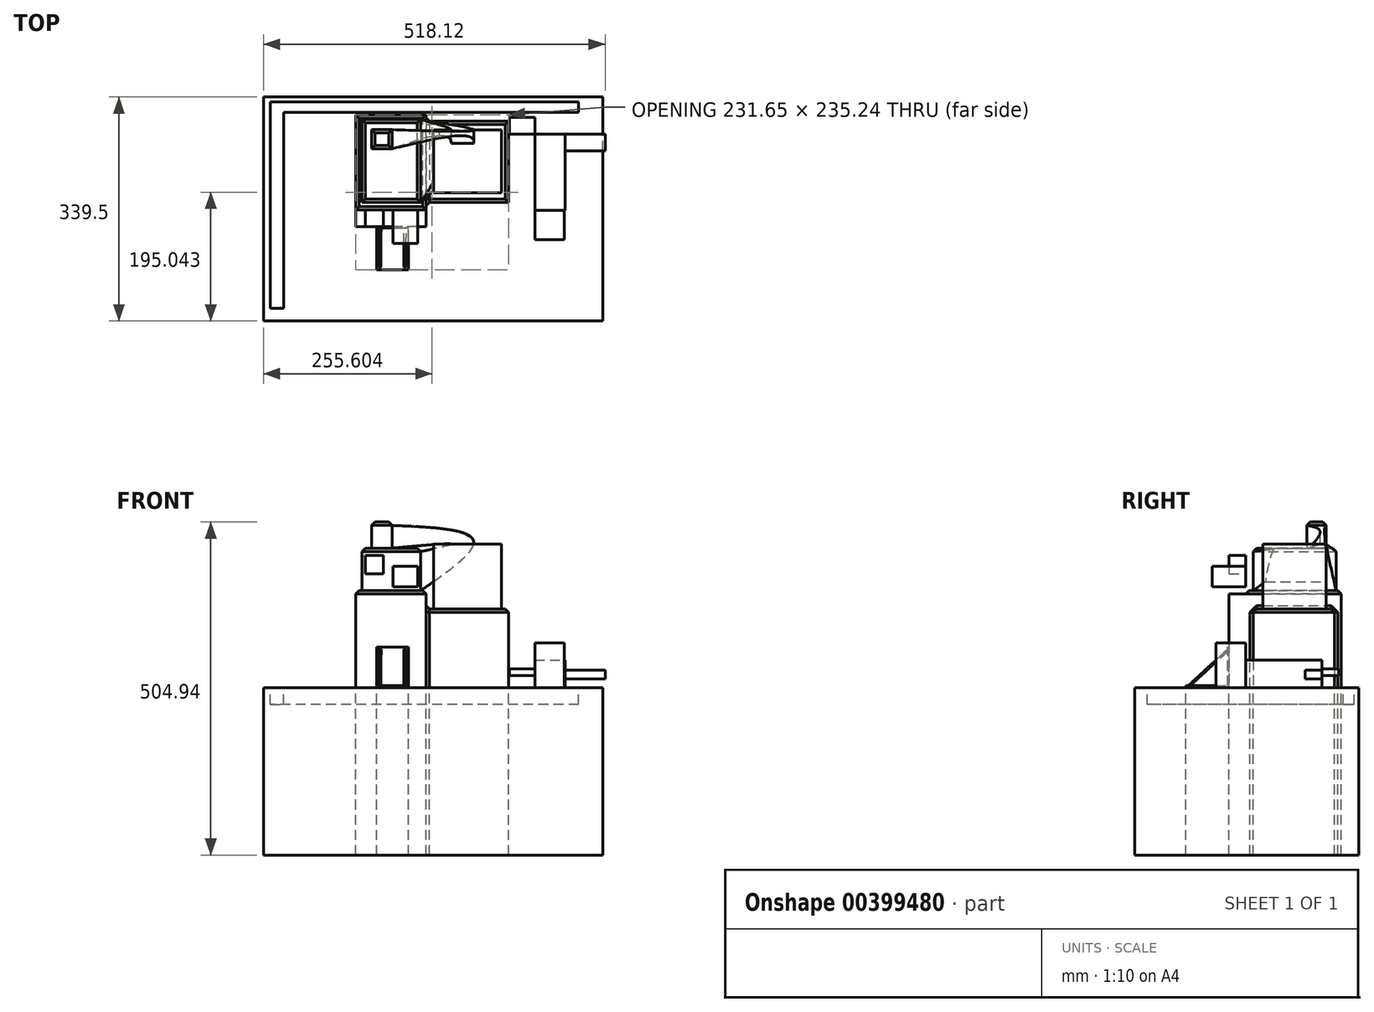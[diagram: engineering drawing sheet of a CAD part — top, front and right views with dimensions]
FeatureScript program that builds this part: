
annotation { "Feature Type Name" : "Feature", "Feature Type Description" : "" }
export const myFeature = defineFeature(function(context is Context, id is Id, definition is map)
    precondition{}
    {
        {
            var Q0;
            Q0=qCreatedBy(makeId("Right.planeOp"),FACE);
            var sketch = newSketch(context, id + "F0", { "sketchPlane" : qUnion([Q0])});
            skLineSegment(sketch, "E0.bottom", {"start": v(-92.5, 57.27) * mm, "end": v(51.8, 57.27) * mm});
            skLineSegment(sketch, "E0.top", {"start": v(-92.5, -89.79) * mm, "end": v(51.8, -89.79) * mm});
            skLineSegment(sketch, "E0.left", {"start": v(-92.5, 57.27) * mm, "end": v(-92.5, -89.79) * mm});
            skLineSegment(sketch, "E0.right", {"start": v(51.8, 57.27) * mm, "end": v(51.8, -89.79) * mm});
            skSolve(sketch);
        }
        {
            var Q0;
            Q0=makeQuery(id+"F0.imprint","IMPRINT",FACE,{"disambiguationData":[TD([[makeQuery(id+"F0.imprint","IMPRINT",EDGE,{"derivedFrom":sQuery(id+"F0.wireOp",EDGE,"E0.bottom")}),-1.0]])]});
            extrude(context, id + "F1", {"entities" : qUnion([Q0]), "depth" : 106.93 * mm});
        }
        {
            var Q0;
            Q0=makeQuery(id+"F1.opExtrude","CAP_EDGE",EDGE,{"disambiguationData":[OSD([sQuery(id+"F0.wireOp",EDGE,"E0.bottom")])],"isStart":true});
            var Q1;
            Q1=makeQuery(id+"F1.opExtrude","CAP_EDGE",EDGE,{"disambiguationData":[OSD([sQuery(id+"F0.wireOp",EDGE,"E0.bottom")])],"isStart":false});
            var Q2;
            Q2=makeQuery(id+"F1.opExtrude","SWEPT_EDGE",EDGE,{"disambiguationData":[OSD([sQuery(id+"F0.wireOp",EDGE,"E0.bottom"),sQuery(id+"F0.wireOp",EDGE,"E0.left")])]});
            var Q3;
            Q3=makeQuery(id+"F1.opExtrude","SWEPT_EDGE",EDGE,{"disambiguationData":[OSD([sQuery(id+"F0.wireOp",EDGE,"E0.bottom"),sQuery(id+"F0.wireOp",EDGE,"E0.right")])]});
            chamfer(context, id + "F2", {"entities" : qUnion([Q0, Q1, Q2, Q3]), "width" : 5.08 * mm, "tangentPropagation" : true});
        }
        {
            var Q0;
            Q0=makeQuery(id+"F1.opExtrude","SWEPT_FACE",FACE,{"disambiguationData":[OSD([sQuery(id+"F0.wireOp",EDGE,"E0.bottom")])]});
            var sketch = newSketch(context, id + "F3", { "sketchPlane" : qUnion([Q0])});
            skLineSegment(sketch, "E1.bottom", {"start": v(9.85, 44.45) * mm, "end": v(98.73, 44.45) * mm});
            skLineSegment(sketch, "E1.top", {"start": v(9.85, -81.23) * mm, "end": v(98.73, -81.23) * mm});
            skLineSegment(sketch, "E1.left", {"start": v(9.85, 44.45) * mm, "end": v(9.85, -81.23) * mm});
            skLineSegment(sketch, "E1.right", {"start": v(98.73, 44.45) * mm, "end": v(98.73, -81.23) * mm});
            skSolve(sketch);
        }
        {
            var Q0;
            Q0=makeQuery(id+"F3.imprint","IMPRINT",FACE,{"disambiguationData":[TD([[makeQuery(id+"F3.imprint","IMPRINT",EDGE,{"derivedFrom":sQuery(id+"F3.wireOp",EDGE,"E1.bottom")}),-1.0]])]});
            extrude(context, id + "F4", {"entities" : qUnion([Q0]), "operationType" : NewBodyOperationType.ADD, "depth" : 64.26 * mm});
        }
        {
            var Q0;
            Q0=makeQuery(id+"F1.opExtrude","CAP_FACE",FACE,{"disambiguationData":[OSD([sQuery(id+"F0.wireOp",EDGE,"E0.bottom"),sQuery(id+"F0.wireOp",EDGE,"E0.top"),sQuery(id+"F0.wireOp",EDGE,"E0.left"),sQuery(id+"F0.wireOp",EDGE,"E0.right")])],"isStart":false});
            var sketch = newSketch(context, id + "F5", { "sketchPlane" : qUnion([Q0])});
            skLineSegment(sketch, "E2.bottom", {"start": v(-81.17, 29.06) * mm, "end": v(42.13, 29.06) * mm});
            skLineSegment(sketch, "E2.top", {"start": v(-81.17, -89.79) * mm, "end": v(42.13, -89.79) * mm});
            skLineSegment(sketch, "E2.left", {"start": v(-81.17, 29.06) * mm, "end": v(-81.17, -89.79) * mm});
            skLineSegment(sketch, "E2.right", {"start": v(42.13, 29.06) * mm, "end": v(42.13, -89.79) * mm});
            skSolve(sketch);
        }
        {
            var Q0;
            Q0=makeQuery(id+"F5.imprint","IMPRINT",FACE,{"disambiguationData":[TD([[makeQuery(id+"F5.imprint","IMPRINT",EDGE,{"derivedFrom":sQuery(id+"F5.wireOp",EDGE,"E2.bottom")}),-1.0]])]});
            extrude(context, id + "F6", {"entities" : qUnion([Q0]), "operationType" : NewBodyOperationType.ADD, "depth" : 124.7 * mm});
        }
        {
            var Q0;
            Q0=makeQuery(id+"F6.opExtrude","SWEPT_EDGE",EDGE,{"disambiguationData":[OSD([sQuery(id+"F5.wireOp",EDGE,"E2.bottom"),sQuery(id+"F5.wireOp",EDGE,"E2.right")])]});
            var Q1;
            Q1=makeQuery(id+"F6.opExtrude","SWEPT_FACE",FACE,{"disambiguationData":[OSD([sQuery(id+"F5.wireOp",EDGE,"E2.bottom")])]});
            chamfer(context, id + "F7", {"entities" : qUnion([Q0, Q1]), "width" : 5.08 * mm, "tangentPropagation" : true});
        }
        {
            var Q0;
            Q0=makeQuery(id+"F4.opExtrude","CAP_EDGE",EDGE,{"disambiguationData":[OSD([sQuery(id+"F3.wireOp",EDGE,"E1.left")])],"isStart":false});
            var Q1;
            Q1=makeQuery(id+"F4.opExtrude","CAP_EDGE",EDGE,{"disambiguationData":[OSD([sQuery(id+"F3.wireOp",EDGE,"E1.bottom")])],"isStart":false});
            var Q2;
            Q2=makeQuery(id+"F4.opExtrude","CAP_EDGE",EDGE,{"disambiguationData":[OSD([sQuery(id+"F3.wireOp",EDGE,"E1.right")])],"isStart":false});
            var Q3;
            Q3=makeQuery(id+"F4.opExtrude","CAP_EDGE",EDGE,{"disambiguationData":[OSD([sQuery(id+"F3.wireOp",EDGE,"E1.top")])],"isStart":false});
            chamfer(context, id + "F8", {"entities" : qUnion([Q0, Q1, Q2, Q3]), "width" : 5.08 * mm, "tangentPropagation" : true});
        }
        {
            var Q0;
            Q0=makeQuery(id+"F6.opExtrude","SWEPT_FACE",FACE,{"disambiguationData":[OSD([sQuery(id+"F5.wireOp",EDGE,"E2.bottom")])]});
            var sketch = newSketch(context, id + "F9", { "sketchPlane" : qUnion([Q0])});
            skLineSegment(sketch, "E3.bottom", {"start": v(118.13, 28.97) * mm, "end": v(221, 28.97) * mm});
            skLineSegment(sketch, "E3.top", {"start": v(118.13, -66.69) * mm, "end": v(221, -66.69) * mm});
            skLineSegment(sketch, "E3.left", {"start": v(118.13, 28.97) * mm, "end": v(118.13, -66.69) * mm});
            skLineSegment(sketch, "E3.right", {"start": v(221, 28.97) * mm, "end": v(221, -66.69) * mm});
            skSolve(sketch);
        }
        {
            var Q0;
            Q0=makeQuery(id+"F9.imprint","IMPRINT",FACE,{"disambiguationData":[TD([[makeQuery(id+"F9.imprint","IMPRINT",EDGE,{"derivedFrom":sQuery(id+"F9.wireOp",EDGE,"E3.bottom")}),-1.0]])]});
            extrude(context, id + "F10", {"entities" : qUnion([Q0]), "operationType" : NewBodyOperationType.ADD, "depth" : 98.55 * mm});
        }
        {
            var Q0;
            Q0=makeQuery(id+"F1.opExtrude","SWEPT_FACE",FACE,{"disambiguationData":[OSD([sQuery(id+"F0.wireOp",EDGE,"E0.left")])]});
            var sketch = newSketch(context, id + "F11", { "sketchPlane" : qUnion([Q0])});
            skLineSegment(sketch, "E4.bottom", {"start": v(32.69, -89.79) * mm, "end": v(72.97, -89.79) * mm});
            skLineSegment(sketch, "E4.top", {"start": v(32.69, -32.08) * mm, "end": v(72.97, -32.08) * mm});
            skLineSegment(sketch, "E4.left", {"start": v(32.69, -89.79) * mm, "end": v(32.69, -32.08) * mm});
            skLineSegment(sketch, "E4.right", {"start": v(72.97, -89.79) * mm, "end": v(72.97, -32.08) * mm});
            skSolve(sketch);
        }
        {
            var Q0;
            Q0=makeQuery(id+"F11.imprint","IMPRINT",FACE,{"disambiguationData":[TD([[makeQuery(id+"F11.imprint","IMPRINT",EDGE,{"derivedFrom":sQuery(id+"F11.wireOp",EDGE,"E4.top")}),1.0]])]});
            var sketch = newSketch(context, id + "F12", { "sketchPlane" : qUnion([Q0])});
            skCircle(sketch, "E5", {"center": v(67.26, -59.23) * mm, "radius": 2 * mm});
            skSolve(sketch);
        }
        {
            var Q0;
            Q0=makeQuery(id+"F11.imprint","IMPRINT",FACE,{"disambiguationData":[TD([[makeQuery(id+"F11.imprint","IMPRINT",EDGE,{"derivedFrom":sQuery(id+"F11.wireOp",EDGE,"E4.bottom")}),-1.0]])]});
            extrude(context, id + "F13", {"entities" : qUnion([Q0]), "operationType" : NewBodyOperationType.ADD, "depth" : 25.4 * mm});
        }
        {
            var Q0;
            Q0=makeQuery(id+"F12.imprint","IMPRINT",FACE,{"disambiguationData":[TD([[makeQuery(id+"F12.imprint","IMPRINT",EDGE,{"derivedFrom":makeQuery(id+"F11.imprint","IMPRINT",EDGE,{"derivedFrom":sQuery(id+"F11.wireOp",EDGE,"E4.top")})}),1.0]])]});
            var sketch = newSketch(context, id + "F14", { "sketchPlane" : qUnion([Q0])});
            skLineSegment(sketch, "E6.bottom", {"start": v(9.26, 44.2) * mm, "end": v(44.69, 44.2) * mm});
            skLineSegment(sketch, "E6.top", {"start": v(9.26, 14.2) * mm, "end": v(44.69, 14.2) * mm});
            skLineSegment(sketch, "E6.left", {"start": v(9.26, 44.2) * mm, "end": v(9.26, 14.2) * mm});
            skLineSegment(sketch, "E6.right", {"start": v(44.69, 44.2) * mm, "end": v(44.69, 14.2) * mm});
            skLineSegment(sketch, "E7.bottom", {"start": v(65.26, 42.77) * mm, "end": v(94.4, 42.77) * mm});
            skLineSegment(sketch, "E7.top", {"start": v(65.26, 12.77) * mm, "end": v(94.4, 12.77) * mm});
            skLineSegment(sketch, "E7.left", {"start": v(65.26, 42.77) * mm, "end": v(65.26, 12.77) * mm});
            skLineSegment(sketch, "E7.right", {"start": v(94.4, 42.77) * mm, "end": v(94.4, 12.77) * mm});
            skLineSegment(sketch, "E8.bottom", {"start": v(119.82, 12.77) * mm, "end": v(145.82, 12.77) * mm});
            skLineSegment(sketch, "E8.top", {"start": v(119.82, -15.23) * mm, "end": v(145.82, -15.23) * mm});
            skLineSegment(sketch, "E8.left", {"start": v(119.82, 12.77) * mm, "end": v(119.82, -15.23) * mm});
            skLineSegment(sketch, "E8.right", {"start": v(145.82, 12.77) * mm, "end": v(145.82, -15.23) * mm});
            skLineSegment(sketch, "E9.bottom", {"start": v(178.96, -31.51) * mm, "end": v(210.68, -31.51) * mm});
            skLineSegment(sketch, "E9.top", {"start": v(178.96, -55.23) * mm, "end": v(210.68, -55.23) * mm});
            skLineSegment(sketch, "E9.left", {"start": v(178.96, -31.51) * mm, "end": v(178.96, -55.23) * mm});
            skLineSegment(sketch, "E9.right", {"start": v(210.68, -31.51) * mm, "end": v(210.68, -55.23) * mm});
            skLineSegment(sketch, "E10.bottom", {"start": v(122.4, 125.9) * mm, "end": v(153.82, 125.9) * mm});
            skLineSegment(sketch, "E10.top", {"start": v(122.4, 91.34) * mm, "end": v(153.82, 91.34) * mm});
            skLineSegment(sketch, "E10.left", {"start": v(122.4, 125.9) * mm, "end": v(122.4, 91.34) * mm});
            skLineSegment(sketch, "E10.right", {"start": v(153.82, 125.9) * mm, "end": v(153.82, 91.34) * mm});
            skLineSegment(sketch, "E11.bottom", {"start": v(171.82, 79.05) * mm, "end": v(204.96, 79.05) * mm});
            skLineSegment(sketch, "E11.top", {"start": v(171.82, 42.2) * mm, "end": v(204.96, 42.2) * mm});
            skLineSegment(sketch, "E11.left", {"start": v(171.82, 79.05) * mm, "end": v(171.82, 42.2) * mm});
            skLineSegment(sketch, "E11.right", {"start": v(204.96, 79.05) * mm, "end": v(204.96, 42.2) * mm});
            skLineSegment(sketch, "E12.bottom", {"start": v(204.96, 42.2) * mm, "end": v(214.96, 42.2) * mm});
            skLineSegment(sketch, "E12.top", {"start": v(204.96, 53.05) * mm, "end": v(214.96, 53.05) * mm});
            skLineSegment(sketch, "E12.left", {"start": v(204.96, 42.2) * mm, "end": v(204.96, 53.05) * mm});
            skLineSegment(sketch, "E12.right", {"start": v(214.96, 42.2) * mm, "end": v(214.96, 53.05) * mm});
            skLineSegment(sketch, "E13.bottom", {"start": v(214.96, 53.05) * mm, "end": v(204.96, 53.05) * mm});
            skLineSegment(sketch, "E13.top", {"start": v(214.96, 79.05) * mm, "end": v(204.96, 79.05) * mm});
            skLineSegment(sketch, "E13.left", {"start": v(214.96, 53.05) * mm, "end": v(214.96, 79.05) * mm});
            skLineSegment(sketch, "E13.right", {"start": v(204.96, 53.05) * mm, "end": v(204.96, 79.05) * mm});
            skLineSegment(sketch, "E14.bottom", {"start": v(14.97, 110.48) * mm, "end": v(42.11, 110.48) * mm});
            skLineSegment(sketch, "E14.top", {"start": v(14.97, 82.48) * mm, "end": v(42.11, 82.48) * mm});
            skLineSegment(sketch, "E14.left", {"start": v(14.97, 110.48) * mm, "end": v(14.97, 82.48) * mm});
            skLineSegment(sketch, "E14.right", {"start": v(42.11, 110.48) * mm, "end": v(42.11, 82.48) * mm});
            skLineSegment(sketch, "E15.bottom", {"start": v(56.68, 94.2) * mm, "end": v(94.11, 94.2) * mm});
            skLineSegment(sketch, "E15.top", {"start": v(56.68, 62.77) * mm, "end": v(94.11, 62.77) * mm});
            skLineSegment(sketch, "E15.left", {"start": v(56.68, 94.2) * mm, "end": v(56.68, 62.77) * mm});
            skLineSegment(sketch, "E15.right", {"start": v(94.11, 94.2) * mm, "end": v(94.11, 62.77) * mm});
            skLineSegment(sketch, "E16", {"start": v(28.54, 110.48) * mm, "end": v(28.54, 82.48) * mm});
            skLineSegment(sketch, "E17", {"start": v(14.97, 96.48) * mm, "end": v(42.11, 96.48) * mm});
            skLineSegment(sketch, "E18", {"start": v(56.68, 78.48) * mm, "end": v(94.11, 78.48) * mm});
            skLineSegment(sketch, "E19", {"start": v(75.4, 94.2) * mm, "end": v(75.4, 62.77) * mm});
            skLineSegment(sketch, "E20", {"start": v(138.1, 125.9) * mm, "end": v(138.1, 91.34) * mm});
            skLineSegment(sketch, "E21", {"start": v(122.4, 106.2) * mm, "end": v(153.82, 106.2) * mm});
            skLineSegment(sketch, "E22", {"start": v(171.82, 60.62) * mm, "end": v(204.96, 60.62) * mm});
            skLineSegment(sketch, "E23", {"start": v(188.4, 79.05) * mm, "end": v(188.4, 44.48) * mm});
            skLineSegment(sketch, "E24", {"start": v(209.96, 79.05) * mm, "end": v(209.96, 42.2) * mm});
            skLineSegment(sketch, "E25", {"start": v(204.96, 62.77) * mm, "end": v(214.96, 62.77) * mm});
            skLineSegment(sketch, "E26", {"start": v(213.82, 63.9) * mm, "end": v(214.96, 62.77) * mm});
            skLineSegment(sketch, "E27", {"start": v(119.82, -3.52) * mm, "end": v(148.4, -3.52) * mm});
            skLineSegment(sketch, "E28", {"start": v(132.82, 12.77) * mm, "end": v(132.82, -15.23) * mm});
            skLineSegment(sketch, "E29", {"start": v(178.96, -45.51) * mm, "end": v(210.68, -45.51) * mm});
            skLineSegment(sketch, "E30", {"start": v(194.82, -31.51) * mm, "end": v(194.82, -55.23) * mm});
            skLineSegment(sketch, "E31", {"start": v(79.83, 42.77) * mm, "end": v(79.83, 12.77) * mm});
            skLineSegment(sketch, "E32", {"start": v(65.26, 27.77) * mm, "end": v(94.4, 27.77) * mm});
            skLineSegment(sketch, "E33", {"start": v(9.26, 29.2) * mm, "end": v(44.69, 29.2) * mm});
            skLineSegment(sketch, "E34", {"start": v(26.97, 44.2) * mm, "end": v(26.97, 14.2) * mm});
            skSolve(sketch);
        }
        {
            var Q0;
            {var subQ0=sQuery(id+"F14.wireOp",EDGE,"E14.right");var subQ1=sQuery(id+"F14.wireOp",EDGE,"E14.bottom");var subQ2=makeQuery(id+"F14.imprint","INTERSECT",VERTEX,{"derivedFrom":[subQ1,subQ0]});Q0=makeQuery(id+"F14.imprint","IMPRINT",FACE,{"disambiguationData":[TD([[makeQuery(id+"F14.imprint","IMPRINT",EDGE,{"disambiguationData":[TD([[subQ2,1.0]])],"derivedFrom":subQ1}),-1.0]])]});}
            var Q1;
            {var subQ0=sQuery(id+"F14.wireOp",EDGE,"E14.left");var subQ1=sQuery(id+"F14.wireOp",EDGE,"E14.top");var subQ2=makeQuery(id+"F14.imprint","INTERSECT",VERTEX,{"derivedFrom":[subQ1,subQ0]});Q1=makeQuery(id+"F14.imprint","IMPRINT",FACE,{"disambiguationData":[TD([[makeQuery(id+"F14.imprint","IMPRINT",EDGE,{"disambiguationData":[TD([[subQ2,-1.0]])],"derivedFrom":subQ1}),1.0]])]});}
            var Q2;
            {var subQ0=sQuery(id+"F14.wireOp",EDGE,"E14.right");var subQ1=sQuery(id+"F14.wireOp",EDGE,"E14.top");var subQ2=makeQuery(id+"F14.imprint","INTERSECT",VERTEX,{"derivedFrom":[subQ1,subQ0]});Q2=makeQuery(id+"F14.imprint","IMPRINT",FACE,{"disambiguationData":[TD([[makeQuery(id+"F14.imprint","IMPRINT",EDGE,{"disambiguationData":[TD([[subQ2,1.0]])],"derivedFrom":subQ1}),1.0]])]});}
            var Q3;
            {var subQ0=sQuery(id+"F14.wireOp",EDGE,"E14.left");var subQ1=sQuery(id+"F14.wireOp",EDGE,"E14.bottom");var subQ2=makeQuery(id+"F14.imprint","INTERSECT",VERTEX,{"derivedFrom":[subQ1,subQ0]});Q3=makeQuery(id+"F14.imprint","IMPRINT",FACE,{"disambiguationData":[TD([[makeQuery(id+"F14.imprint","IMPRINT",EDGE,{"disambiguationData":[TD([[subQ2,-1.0]])],"derivedFrom":subQ1}),-1.0]])]});}
            var Q4;
            {var subQ0=sQuery(id+"F14.wireOp",EDGE,"E15.left");var subQ1=sQuery(id+"F14.wireOp",EDGE,"E15.bottom");var subQ2=makeQuery(id+"F14.imprint","INTERSECT",VERTEX,{"derivedFrom":[subQ1,subQ0]});Q4=makeQuery(id+"F14.imprint","IMPRINT",FACE,{"disambiguationData":[TD([[makeQuery(id+"F14.imprint","IMPRINT",EDGE,{"disambiguationData":[TD([[subQ2,-1.0]])],"derivedFrom":subQ1}),-1.0]])]});}
            var Q5;
            {var subQ0=sQuery(id+"F14.wireOp",EDGE,"E15.right");var subQ1=sQuery(id+"F14.wireOp",EDGE,"E15.bottom");var subQ2=makeQuery(id+"F14.imprint","INTERSECT",VERTEX,{"derivedFrom":[subQ1,subQ0]});Q5=makeQuery(id+"F14.imprint","IMPRINT",FACE,{"disambiguationData":[TD([[makeQuery(id+"F14.imprint","IMPRINT",EDGE,{"disambiguationData":[TD([[subQ2,1.0]])],"derivedFrom":subQ1}),-1.0]])]});}
            var Q6;
            {var subQ0=sQuery(id+"F14.wireOp",EDGE,"E15.left");var subQ1=sQuery(id+"F14.wireOp",EDGE,"E15.top");var subQ2=makeQuery(id+"F14.imprint","INTERSECT",VERTEX,{"derivedFrom":[subQ1,subQ0]});Q6=makeQuery(id+"F14.imprint","IMPRINT",FACE,{"disambiguationData":[TD([[makeQuery(id+"F14.imprint","IMPRINT",EDGE,{"disambiguationData":[TD([[subQ2,-1.0]])],"derivedFrom":subQ1}),1.0]])]});}
            var Q7;
            {var subQ0=sQuery(id+"F14.wireOp",EDGE,"E15.right");var subQ1=sQuery(id+"F14.wireOp",EDGE,"E15.top");var subQ2=makeQuery(id+"F14.imprint","INTERSECT",VERTEX,{"derivedFrom":[subQ1,subQ0]});Q7=makeQuery(id+"F14.imprint","IMPRINT",FACE,{"disambiguationData":[TD([[makeQuery(id+"F14.imprint","IMPRINT",EDGE,{"disambiguationData":[TD([[subQ2,1.0]])],"derivedFrom":subQ1}),1.0]])]});}
            var Q8;
            Q8=makeQuery(id+"F12.imprint","IMPRINT",FACE,{"disambiguationData":[TD([[makeQuery(id+"F12.imprint","IMPRINT",EDGE,{"derivedFrom":makeQuery(id+"F11.imprint","IMPRINT",EDGE,{"derivedFrom":sQuery(id+"F11.wireOp",EDGE,"E4.top")})}),1.0]])]});
            extrude(context, id + "F15", {"entities" : qUnion([Q0, Q1, Q2, Q3, Q4, Q5, Q6, Q7, Q8]), "operationType" : NewBodyOperationType.ADD, "depth" : 25.4 * mm});
        }
        {
            var Q0;
            Q0=makeQuery(id+"F15.opExtrude","CAP_FACE",FACE,{"disambiguationData":[OSD([sQuery(id+"F14.wireOp",EDGE,"E15.bottom"),sQuery(id+"F14.wireOp",EDGE,"E15.top"),sQuery(id+"F14.wireOp",EDGE,"E15.left"),sQuery(id+"F14.wireOp",EDGE,"E15.right")])],"isStart":false});
            extrude(context, id + "F16", {"entities" : qUnion([Q0]), "operationType" : NewBodyOperationType.ADD, "depth" : 25.4 * mm});
        }
        {
            var Q0;
            Q0=makeQuery(id+"F4.opExtrude","CAP_FACE",FACE,{"disambiguationData":[OSD([sQuery(id+"F3.wireOp",EDGE,"E1.bottom"),sQuery(id+"F3.wireOp",EDGE,"E1.top"),sQuery(id+"F3.wireOp",EDGE,"E1.left"),sQuery(id+"F3.wireOp",EDGE,"E1.right")])],"isStart":false});
            var sketch = newSketch(context, id + "F17", { "sketchPlane" : qUnion([Q0])});
            skLineSegment(sketch, "E35.bottom", {"start": v(24.3, 29.25) * mm, "end": v(55.31, 29.25) * mm});
            skLineSegment(sketch, "E35.top", {"start": v(24.3, 0.27) * mm, "end": v(55.31, 0.27) * mm});
            skLineSegment(sketch, "E35.left", {"start": v(24.3, 29.25) * mm, "end": v(24.3, 0.27) * mm});
            skLineSegment(sketch, "E35.right", {"start": v(55.31, 29.25) * mm, "end": v(55.31, 0.27) * mm});
            skSolve(sketch);
        }
        {
            var Q0;
            Q0=makeQuery(id+"F17.imprint","IMPRINT",FACE,{"disambiguationData":[TD([[makeQuery(id+"F17.imprint","IMPRINT",EDGE,{"derivedFrom":sQuery(id+"F17.wireOp",EDGE,"E35.bottom")}),-1.0]])]});
            extrude(context, id + "F18", {"entities" : qUnion([Q0]), "operationType" : NewBodyOperationType.ADD, "depth" : 39.62 * mm});
        }
        {
            var Q0;
            Q0=makeQuery(id+"F18.opExtrude","CAP_EDGE",EDGE,{"disambiguationData":[OSD([sQuery(id+"F17.wireOp",EDGE,"E35.right")])],"isStart":false});
            chamfer(context, id + "F19", {"entities" : qUnion([Q0]), "width" : 5.08 * mm, "tangentPropagation" : true});
        }
        {
            var Q0;
            Q0=makeQuery(id+"F18.opExtrude","CAP_EDGE",EDGE,{"disambiguationData":[OSD([sQuery(id+"F17.wireOp",EDGE,"E35.bottom")])],"isStart":false});
            var Q1;
            Q1=makeQuery(id+"F18.opExtrude","CAP_EDGE",EDGE,{"disambiguationData":[OSD([sQuery(id+"F17.wireOp",EDGE,"E35.left")])],"isStart":false});
            var Q2;
            Q2=makeQuery(id+"F18.opExtrude","CAP_EDGE",EDGE,{"disambiguationData":[OSD([sQuery(id+"F17.wireOp",EDGE,"E35.top")])],"isStart":false});
            chamfer(context, id + "F20", {"entities" : qUnion([Q0, Q1, Q2]), "width" : 5.08 * mm, "tangentPropagation" : true});
        }
        {
            var Q0;
            {var subQ0=sQuery(id+"F11.wireOp",EDGE,"E4.right");var subQ1=sQuery(id+"F11.wireOp",EDGE,"E4.left");var subQ2=sQuery(id+"F11.wireOp",EDGE,"E4.top");Q0=makeQuery(id+"F15.boolean.opBoolean","MERGE",FACE,{"derivedFrom":[makeQuery(id+"F13.opExtrude","CAP_FACE",FACE,{"disambiguationData":[OSD([sQuery(id+"F11.wireOp",EDGE,"E4.bottom"),subQ2,subQ1,subQ0])],"isStart":false}),makeQuery(id+"F15.opExtrude","CAP_FACE",FACE,{"disambiguationData":[OSD([sQuery(id+"F0.wireOp",EDGE,"E0.bottom"),sQuery(id+"F0.wireOp",EDGE,"E0.top"),sQuery(id+"F0.wireOp",EDGE,"E0.left"),subQ2,subQ1,subQ0])],"isStart":false})]});}
            var sketch = newSketch(context, id + "F21", { "sketchPlane" : qUnion([Q0])});
            skLineSegment(sketch, "E36.bottom", {"start": v(31.4, -89.79) * mm, "end": v(31.73, -89.79) * mm});
            skLineSegment(sketch, "E36.top", {"start": v(31.4, -28.13) * mm, "end": v(31.73, -28.13) * mm});
            skLineSegment(sketch, "E36.left", {"start": v(31.4, -89.79) * mm, "end": v(31.4, -28.13) * mm});
            skLineSegment(sketch, "E36.right", {"start": v(31.73, -89.79) * mm, "end": v(31.73, -28.13) * mm});
            skLineSegment(sketch, "E37.bottom", {"start": v(31.73, -28.13) * mm, "end": v(79.88, -28.13) * mm});
            skLineSegment(sketch, "E37.top", {"start": v(31.73, -89.79) * mm, "end": v(79.88, -89.79) * mm});
            skLineSegment(sketch, "E37.left", {"start": v(31.73, -28.13) * mm, "end": v(31.73, -89.79) * mm});
            skLineSegment(sketch, "E37.right", {"start": v(79.88, -28.13) * mm, "end": v(79.88, -89.79) * mm});
            skCircle(sketch, "E38", {"center": v(74.6, -59.46) * mm, "radius": 2 * mm});
            skSolve(sketch);
        }
        {
            var Q0;
            Q0=makeQuery(id+"F21.imprint","IMPRINT",FACE,{"disambiguationData":[TD([[makeQuery(id+"F21.imprint","IMPRINT",EDGE,{"derivedFrom":sQuery(id+"F21.wireOp",EDGE,"E37.bottom")}),-1.0]])]});
            var Q1;
            Q1=makeQuery(id+"F21.imprint","IMPRINT",FACE,{"disambiguationData":[TD([[makeQuery(id+"F21.imprint","IMPRINT",EDGE,{"derivedFrom":sQuery(id+"F21.wireOp",EDGE,"E38")}),1.0]])]});
            extrude(context, id + "F22", {"entities" : qUnion([Q0, Q1]), "operationType" : NewBodyOperationType.ADD, "depth" : 2.03 * mm});
        }
        {
            var Q0;
            Q0=makeQuery(id+"F10.opExtrude","CAP_FACE",FACE,{"disambiguationData":[OSD([sQuery(id+"F9.wireOp",EDGE,"E3.bottom"),sQuery(id+"F9.wireOp",EDGE,"E3.top"),sQuery(id+"F9.wireOp",EDGE,"E3.left"),sQuery(id+"F9.wireOp",EDGE,"E3.right")])],"isStart":false});
            var sketch = newSketch(context, id + "F23", { "sketchPlane" : qUnion([Q0])});
            skLineSegment(sketch, "E39.bottom", {"start": v(136.73, -34.68) * mm, "end": v(196.42, -34.68) * mm});
            skLineSegment(sketch, "E39.top", {"start": v(136.73, -66.69) * mm, "end": v(196.42, -66.69) * mm});
            skLineSegment(sketch, "E39.left", {"start": v(136.73, -34.68) * mm, "end": v(136.73, -66.69) * mm});
            skLineSegment(sketch, "E39.right", {"start": v(196.42, -34.68) * mm, "end": v(196.42, -66.69) * mm});
            skLineSegment(sketch, "E40.bottom", {"start": v(144.96, 28.97) * mm, "end": v(179.05, 28.97) * mm});
            skLineSegment(sketch, "E40.top", {"start": v(144.96, 8.3) * mm, "end": v(179.05, 8.3) * mm});
            skLineSegment(sketch, "E40.left", {"start": v(144.96, 28.97) * mm, "end": v(144.96, 8.3) * mm});
            skLineSegment(sketch, "E40.right", {"start": v(179.05, 28.97) * mm, "end": v(179.05, 8.3) * mm});
            skSolve(sketch);
        }
        {
            var Q1;
            Q1=makeQuery(id+"F18.opExtrude","SWEPT_FACE",FACE,{"disambiguationData":[OSD([sQuery(id+"F17.wireOp",EDGE,"E35.right")])]});
            var Q2;
            Q2=makeQuery(id+"F23.imprint","IMPRINT",FACE,{"disambiguationData":[TD([[makeQuery(id+"F23.imprint","IMPRINT",EDGE,{"derivedFrom":sQuery(id+"F23.wireOp",EDGE,"E40.bottom")}),-1.0]])]});
            var Q3;
            Q3=makeQuery(id+"F4.opExtrude","SWEPT_FACE",FACE,{"disambiguationData":[OSD([sQuery(id+"F3.wireOp",EDGE,"E1.right")])]});
            loft(context, id + "F24", {"operationType" : NewBodyOperationType.ADD, "sheetProfilesArray" : [{ "sheetProfileEntities" : qUnion([Q1]) }, { "sheetProfileEntities" : qUnion([Q2]) }, { "sheetProfileEntities" : qUnion([Q3]) }]});
        }
        {
            var Q0;
            Q0=makeQuery(id+"F22.opExtrude","CAP_FACE",FACE,{"disambiguationData":[OSD([sQuery(id+"F21.wireOp",EDGE,"E37.bottom"),sQuery(id+"F21.wireOp",EDGE,"E37.top"),sQuery(id+"F21.wireOp",EDGE,"E37.left"),sQuery(id+"F21.wireOp",EDGE,"E37.right")])],"isStart":false});
            var sketch = newSketch(context, id + "F25", { "sketchPlane" : qUnion([Q0])});
            skLineSegment(sketch, "E41.bottom", {"start": v(31.73, -89.79) * mm, "end": v(79.88, -89.79) * mm});
            skLineSegment(sketch, "E41.top", {"start": v(31.73, -86.87) * mm, "end": v(79.88, -86.87) * mm});
            skLineSegment(sketch, "E41.left", {"start": v(31.73, -89.79) * mm, "end": v(31.73, -86.87) * mm});
            skLineSegment(sketch, "E41.right", {"start": v(79.88, -89.79) * mm, "end": v(79.88, -86.87) * mm});
            skSolve(sketch);
        }
        {
            var Q0;
            Q0=makeQuery(id+"F25.imprint","IMPRINT",FACE,{"disambiguationData":[TD([[makeQuery(id+"F25.imprint","IMPRINT",EDGE,{"derivedFrom":sQuery(id+"F25.wireOp",EDGE,"E41.bottom")}),-1.0]])]});
            extrude(context, id + "F26", {"entities" : qUnion([Q0]), "operationType" : NewBodyOperationType.ADD, "depth" : 63.5 * mm});
        }
        {
            var Q0;
            Q0=makeQuery(id+"F22.opExtrude","CAP_FACE",FACE,{"disambiguationData":[OSD([sQuery(id+"F21.wireOp",EDGE,"E37.bottom"),sQuery(id+"F21.wireOp",EDGE,"E37.top"),sQuery(id+"F21.wireOp",EDGE,"E37.left"),sQuery(id+"F21.wireOp",EDGE,"E37.right")])],"isStart":false});
            var sketch = newSketch(context, id + "F27", { "sketchPlane" : qUnion([Q0])});
            skCircle(sketch, "E42", {"center": v(36.81, -33.2) * mm, "radius": 1.9 * mm});
            skCircle(sketch, "E43", {"center": v(74.8, -33.2) * mm, "radius": 1.9 * mm});
            skSolve(sketch);
        }
        {
            var Q0;
            Q0=makeQuery(id+"F26.opExtrude","SWEPT_FACE",FACE,{"disambiguationData":[OSD([sQuery(id+"F25.wireOp",EDGE,"E41.top")])]});
            var sketch = newSketch(context, id + "F28", { "sketchPlane" : qUnion([Q0])});
            skCircle(sketch, "E44", {"center": v(36.81, -178.36) * mm, "radius": 1.46 * mm});
            skCircle(sketch, "E45", {"center": v(74.8, -178.36) * mm, "radius": 1.46 * mm});
            skSolve(sketch);
        }
        {
            var Q1;
            Q1=makeQuery(id+"F28.imprint","IMPRINT",FACE,{"disambiguationData":[TD([[makeQuery(id+"F28.imprint","IMPRINT",EDGE,{"derivedFrom":sQuery(id+"F28.wireOp",EDGE,"E44")}),1.0]])]});
            var Q2;
            Q2=makeQuery(id+"F27.imprint","IMPRINT",FACE,{"disambiguationData":[TD([[makeQuery(id+"F27.imprint","IMPRINT",EDGE,{"derivedFrom":sQuery(id+"F27.wireOp",EDGE,"E42")}),1.0]])]});
            loft(context, id + "F29", {"operationType" : NewBodyOperationType.ADD, "sheetProfilesArray" : [{ "sheetProfileEntities" : qUnion([Q1]) }, { "sheetProfileEntities" : qUnion([Q2]) }]});
        }
        {
            var Q1;
            Q1=makeQuery(id+"F27.imprint","IMPRINT",FACE,{"disambiguationData":[TD([[makeQuery(id+"F27.imprint","IMPRINT",EDGE,{"derivedFrom":sQuery(id+"F27.wireOp",EDGE,"E43")}),1.0]])]});
            var Q2;
            Q2=makeQuery(id+"F28.imprint","IMPRINT",FACE,{"disambiguationData":[TD([[makeQuery(id+"F28.imprint","IMPRINT",EDGE,{"derivedFrom":sQuery(id+"F28.wireOp",EDGE,"E45")}),1.0]])]});
            loft(context, id + "F30", {"operationType" : NewBodyOperationType.ADD, "sheetProfilesArray" : [{ "sheetProfileEntities" : qUnion([Q1]) }, { "sheetProfileEntities" : qUnion([Q2]) }]});
        }
        {
            var Q0;
            {var subQ0=sQuery(id+"F0.wireOp",EDGE,"E0.left");var subQ1=sQuery(id+"F0.wireOp",EDGE,"E0.top");var subQ2=makeQuery(id+"F1.opExtrude","SWEPT_EDGE",EDGE,{"disambiguationData":[OSD([subQ1,subQ0])]});var subQ3=sQuery(id+"F11.wireOp",EDGE,"E4.bottom");Q0=makeQuery(id+"F26.boolean.opBoolean","MERGE",FACE,{"derivedFrom":[makeQuery(id+"F22.boolean.opBoolean","MERGE",FACE,{"derivedFrom":[makeQuery(id+"F15.boolean.opBoolean","MERGE",FACE,{"derivedFrom":[makeQuery(id+"F13.boolean.opBoolean","MERGE",FACE,{"derivedFrom":[makeQuery(id+"F6.boolean.opBoolean","MERGE",FACE,{"derivedFrom":[makeQuery(id+"F1.opExtrude","SWEPT_FACE",FACE,{"disambiguationData":[OSD([subQ1])]}),makeQuery(id+"F6.opExtrude","SWEPT_FACE",FACE,{"disambiguationData":[OSD([sQuery(id+"F5.wireOp",EDGE,"E2.top")])]})]}),makeQuery(id+"F13.opExtrude","SWEPT_FACE",FACE,{"disambiguationData":[OSD([subQ3])]})]}),makeQuery(id+"F15.opExtrude","SWEPT_FACE",FACE,{"disambiguationData":[OSD([subQ1,subQ0]),TDD([makeQuery(id+"F12.imprint","IMPRINT",EDGE,{"derivedFrom":makeQuery(id+"F11.imprint","IMPRINT",EDGE,{"disambiguationData":[TD([[makeQuery(id+"F11.imprint","INTERSECT",VERTEX,{"derivedFrom":[subQ2,makeQuery(id+"F1.opExtrude","CAP_EDGE",EDGE,{"disambiguationData":[OSD([subQ0])],"isStart":true})]}),1.0]])],"derivedFrom":subQ2})})])]}),makeQuery(id+"F15.opExtrude","SWEPT_FACE",FACE,{"disambiguationData":[OSD([subQ1,subQ0]),TDD([makeQuery(id+"F12.imprint","IMPRINT",EDGE,{"derivedFrom":makeQuery(id+"F11.imprint","IMPRINT",EDGE,{"disambiguationData":[TD([[makeQuery(id+"F11.imprint","INTERSECT",VERTEX,{"derivedFrom":[subQ2,makeQuery(id+"F1.opExtrude","CAP_EDGE",EDGE,{"disambiguationData":[OSD([subQ0])],"isStart":false})]}),-1.0]])],"derivedFrom":subQ2})})])]})]}),makeQuery(id+"F22.opExtrude","SWEPT_FACE",FACE,{"disambiguationData":[OSD([sQuery(id+"F21.wireOp",EDGE,"E37.top")])]})]}),makeQuery(id+"F26.opExtrude","SWEPT_FACE",FACE,{"disambiguationData":[OSD([sQuery(id+"F25.wireOp",EDGE,"E41.bottom")])]})]});}
            var sketch = newSketch(context, id + "F31", { "sketchPlane" : qUnion([Q0])});
            skLineSegment(sketch, "E46.bottom", {"start": v(-139.78, 210.06) * mm, "end": v(374.9, 210.06) * mm});
            skLineSegment(sketch, "E46.top", {"start": v(-139.78, -78.64) * mm, "end": v(374.9, -78.64) * mm});
            skLineSegment(sketch, "E46.left", {"start": v(-139.78, 210.06) * mm, "end": v(-139.78, -78.64) * mm});
            skLineSegment(sketch, "E46.right", {"start": v(374.9, 210.06) * mm, "end": v(374.9, -78.64) * mm});
            skSolve(sketch);
        }
        {
            var Q0;
            Q0=makeQuery(id+"F31.imprint","IMPRINT",FACE,{"disambiguationData":[TD([[makeQuery(id+"F31.imprint","IMPRINT",EDGE,{"derivedFrom":sQuery(id+"F31.wireOp",EDGE,"E46.bottom")}),-1.0]])]});
            extrude(context, id + "F32", {"entities" : qUnion([Q0]), "depth" : 254 * mm});
        }
        {
            var Q0;
            Q0=makeQuery(id+"F32.opExtrude","SWEPT_FACE",FACE,{"disambiguationData":[OSD([sQuery(id+"F31.wireOp",EDGE,"E46.bottom")])]});
            var sketch = newSketch(context, id + "F33", { "sketchPlane" : qUnion([Q0])});
            skLineSegment(sketch, "E47.bottom", {"start": v(-139.78, -89.79) * mm, "end": v(374.9, -89.79) * mm});
            skLineSegment(sketch, "E47.top", {"start": v(-139.78, -343.79) * mm, "end": v(374.9, -343.79) * mm});
            skLineSegment(sketch, "E47.left", {"start": v(-139.78, -89.79) * mm, "end": v(-139.78, -343.79) * mm});
            skLineSegment(sketch, "E47.right", {"start": v(374.9, -89.79) * mm, "end": v(374.9, -343.79) * mm});
            skSolve(sketch);
        }
        {
            var Q0;
            Q0=makeQuery(id+"F33.imprint","IMPRINT",FACE,{"disambiguationData":[TD([[makeQuery(id+"F33.imprint","IMPRINT",EDGE,{"derivedFrom":sQuery(id+"F33.wireOp",EDGE,"E47.bottom")}),-1.0]])]});
            extrude(context, id + "F34", {"entities" : qUnion([Q0]), "operationType" : NewBodyOperationType.ADD, "depth" : 50.8 * mm});
        }
        {
            var Q0;
            Q0=makeQuery(id+"F34.boolean.opBoolean","MERGE",FACE,{"derivedFrom":[makeQuery(id+"F32.opExtrude","CAP_FACE",FACE,{"disambiguationData":[OSD([sQuery(id+"F0.wireOp",EDGE,"E0.top"),sQuery(id+"F0.wireOp",EDGE,"E0.left"),sQuery(id+"F0.wireOp",EDGE,"E0.right"),sQuery(id+"F5.wireOp",EDGE,"E2.top"),sQuery(id+"F5.wireOp",EDGE,"E2.left"),sQuery(id+"F5.wireOp",EDGE,"E2.right"),sQuery(id+"F11.wireOp",EDGE,"E4.bottom"),sQuery(id+"F21.wireOp",EDGE,"E36.bottom"),sQuery(id+"F21.wireOp",EDGE,"E37.top"),sQuery(id+"F21.wireOp",EDGE,"E37.left"),sQuery(id+"F21.wireOp",EDGE,"E37.right"),sQuery(id+"F25.wireOp",EDGE,"E41.bottom"),sQuery(id+"F25.wireOp",EDGE,"E41.left"),sQuery(id+"F25.wireOp",EDGE,"E41.right"),sQuery(id+"F31.wireOp",EDGE,"E46.bottom"),sQuery(id+"F31.wireOp",EDGE,"E46.top"),sQuery(id+"F31.wireOp",EDGE,"E46.left"),sQuery(id+"F31.wireOp",EDGE,"E46.right")])],"isStart":true}),makeQuery(id+"F34.opExtrude","SWEPT_FACE",FACE,{"disambiguationData":[OSD([sQuery(id+"F33.wireOp",EDGE,"E47.bottom")])]})]});
            var sketch = newSketch(context, id + "F35", { "sketchPlane" : qUnion([Q0])});
            skLineSegment(sketch, "E48.bottom", {"start": v(-129.38, -221.2) * mm, "end": v(365.47, -221.2) * mm});
            skLineSegment(sketch, "E48.top", {"start": v(-129.38, -241.96) * mm, "end": v(365.47, -241.96) * mm});
            skLineSegment(sketch, "E48.left", {"start": v(-129.38, -221.2) * mm, "end": v(-129.38, -241.96) * mm});
            skLineSegment(sketch, "E48.right", {"start": v(365.47, -221.2) * mm, "end": v(365.47, -241.96) * mm});
            skLineSegment(sketch, "E49.bottom", {"start": v(365.47, -221.2) * mm, "end": v(338.03, -221.2) * mm});
            skLineSegment(sketch, "E49.top", {"start": v(365.47, 55.23) * mm, "end": v(338.03, 55.23) * mm});
            skLineSegment(sketch, "E49.left", {"start": v(365.47, -221.2) * mm, "end": v(365.47, 55.23) * mm});
            skLineSegment(sketch, "E49.right", {"start": v(338.03, -221.2) * mm, "end": v(338.03, 55.23) * mm});
            skLineSegment(sketch, "E50.bottom", {"start": v(338.03, 55.23) * mm, "end": v(365.47, 55.23) * mm});
            skLineSegment(sketch, "E50.top", {"start": v(338.03, 71.63) * mm, "end": v(365.47, 71.63) * mm});
            skLineSegment(sketch, "E50.left", {"start": v(338.03, 55.23) * mm, "end": v(338.03, 71.63) * mm});
            skLineSegment(sketch, "E50.right", {"start": v(365.47, 55.23) * mm, "end": v(365.47, 71.63) * mm});
            skLineSegment(sketch, "E51.bottom", {"start": v(338.03, 71.63) * mm, "end": v(-108.86, 71.63) * mm});
            skLineSegment(sketch, "E51.top", {"start": v(338.03, 55.23) * mm, "end": v(-108.86, 55.23) * mm});
            skLineSegment(sketch, "E51.left", {"start": v(338.03, 71.63) * mm, "end": v(338.03, 55.23) * mm});
            skLineSegment(sketch, "E51.right", {"start": v(-108.86, 71.63) * mm, "end": v(-108.86, 55.23) * mm});
            skLineSegment(sketch, "E52.bottom", {"start": v(-108.86, 71.63) * mm, "end": v(-129.38, 71.63) * mm});
            skLineSegment(sketch, "E52.top", {"start": v(-108.86, -241.96) * mm, "end": v(-129.38, -241.96) * mm});
            skLineSegment(sketch, "E52.left", {"start": v(-108.86, 71.63) * mm, "end": v(-108.86, -241.96) * mm});
            skLineSegment(sketch, "E52.right", {"start": v(-129.38, 71.63) * mm, "end": v(-129.38, -241.96) * mm});
            skSolve(sketch);
        }
        {
            var Q0;
            {var subQ0=sQuery(id+"F35.wireOp",EDGE,"E51.bottom");Q0=makeQuery(id+"F35.imprint","IMPRINT",FACE,{"disambiguationData":[TD([[makeQuery(id+"F35.imprint","IMPRINT",EDGE,{"derivedFrom":subQ0}),1.0]])]});}
            var Q1;
            Q1=makeQuery(id+"F35.imprint","IMPRINT",FACE,{"disambiguationData":[TD([[makeQuery(id+"F35.imprint","IMPRINT",EDGE,{"derivedFrom":sQuery(id+"F35.wireOp",EDGE,"E50.bottom")}),1.0]])]});
            var Q2;
            Q2=makeQuery(id+"F35.imprint","IMPRINT",FACE,{"disambiguationData":[TD([[makeQuery(id+"F35.imprint","IMPRINT",EDGE,{"derivedFrom":sQuery(id+"F35.wireOp",EDGE,"E49.bottom")}),-1.0]])]});
            var Q3;
            {var subQ1=sQuery(id+"F35.wireOp",EDGE,"E48.top");Q3=makeQuery(id+"F35.imprint","IMPRINT",FACE,{"disambiguationData":[TD([[makeQuery(id+"F35.imprint","IMPRINT",EDGE,{"derivedFrom":subQ1}),1.0]])]});}
            var Q4;
            {var subQ5=sQuery(id+"F35.wireOp",EDGE,"E52.top");Q4=makeQuery(id+"F35.imprint","IMPRINT",FACE,{"disambiguationData":[TD([[makeQuery(id+"F35.imprint","IMPRINT",EDGE,{"derivedFrom":subQ5}),-1.0]])]});}
            var Q5;
            {var subQ4=sQuery(id+"F35.wireOp",EDGE,"E52.bottom");Q5=makeQuery(id+"F35.imprint","IMPRINT",FACE,{"disambiguationData":[TD([[makeQuery(id+"F35.imprint","IMPRINT",EDGE,{"derivedFrom":subQ4}),1.0]])]});}
            extrude(context, id + "F36", {"entities" : qUnion([Q0, Q1, Q2, Q3, Q4, Q5]), "operationType" : NewBodyOperationType.REMOVE, "oppositeDirection" : true, "depth" : 25.4 * mm});
        }
        {
            var Q0;
            {var subQ0=sQuery(id+"F21.wireOp",EDGE,"E37.top");var subQ2=sQuery(id+"F0.wireOp",EDGE,"E0.left");var subQ4=sQuery(id+"F0.wireOp",EDGE,"E0.top");var subQ7=sQuery(id+"F11.wireOp",EDGE,"E4.bottom");var subQ20=sQuery(id+"F0.wireOp",EDGE,"E0.right");var subQ21=sQuery(id+"F5.wireOp",EDGE,"E2.top");var subQ23=sQuery(id+"F21.wireOp",EDGE,"E37.left");var subQ30=sQuery(id+"F5.wireOp",EDGE,"E2.left");var subQ31=sQuery(id+"F5.wireOp",EDGE,"E2.right");var subQ33=sQuery(id+"F21.wireOp",EDGE,"E37.right");var subQ34=sQuery(id+"F25.wireOp",EDGE,"E41.bottom");var subQ35=sQuery(id+"F25.wireOp",EDGE,"E41.left");var subQ36=sQuery(id+"F21.wireOp",EDGE,"E36.bottom");var subQ37=sQuery(id+"F25.wireOp",EDGE,"E41.right");Q0=makeQuery(id+"F36.boolean.opBoolean","SPLIT",FACE,{"disambiguationData":[TD([makeQuery(id+"F32.opExtrude","SWEPT_FACE",FACE,{"disambiguationData":[OSD([subQ21])]})])],"derivedFrom":makeQuery(id+"F34.boolean.opBoolean","MERGE",FACE,{"derivedFrom":[makeQuery(id+"F32.opExtrude","CAP_FACE",FACE,{"disambiguationData":[OSD([subQ4,subQ2,subQ20,subQ21,subQ30,subQ31,subQ7,subQ36,subQ0,subQ23,subQ33,subQ34,subQ35,subQ37,sQuery(id+"F31.wireOp",EDGE,"E46.bottom"),sQuery(id+"F31.wireOp",EDGE,"E46.top"),sQuery(id+"F31.wireOp",EDGE,"E46.left"),sQuery(id+"F31.wireOp",EDGE,"E46.right")])],"isStart":true}),makeQuery(id+"F34.opExtrude","SWEPT_FACE",FACE,{"disambiguationData":[OSD([sQuery(id+"F33.wireOp",EDGE,"E47.bottom")])]})]})});}
            var sketch = newSketch(context, id + "F37", { "sketchPlane" : qUnion([Q0])});
            skLineSegment(sketch, "E53.bottom", {"start": v(271.64, -2.85) * mm, "end": v(317.31, -2.85) * mm});
            skLineSegment(sketch, "E53.top", {"start": v(271.64, -92.88) * mm, "end": v(317.31, -92.88) * mm});
            skLineSegment(sketch, "E53.left", {"start": v(271.64, -2.85) * mm, "end": v(271.64, -92.88) * mm});
            skLineSegment(sketch, "E53.right", {"start": v(317.31, -2.85) * mm, "end": v(317.31, -92.88) * mm});
            skSolve(sketch);
        }
        {
            var Q0;
            Q0=makeQuery(id+"F37.imprint","IMPRINT",FACE,{"disambiguationData":[TD([[makeQuery(id+"F37.imprint","IMPRINT",EDGE,{"derivedFrom":sQuery(id+"F37.wireOp",EDGE,"E53.bottom")}),-1.0]])]});
            extrude(context, id + "F38", {"entities" : qUnion([Q0]), "operationType" : NewBodyOperationType.ADD, "depth" : 41.66 * mm});
        }
        {
            var Q0;
            {var subQ0=sQuery(id+"F21.wireOp",EDGE,"E37.top");var subQ2=sQuery(id+"F0.wireOp",EDGE,"E0.left");var subQ4=sQuery(id+"F0.wireOp",EDGE,"E0.top");var subQ7=sQuery(id+"F11.wireOp",EDGE,"E4.bottom");var subQ20=sQuery(id+"F0.wireOp",EDGE,"E0.right");var subQ21=sQuery(id+"F5.wireOp",EDGE,"E2.top");var subQ23=sQuery(id+"F21.wireOp",EDGE,"E37.left");var subQ30=sQuery(id+"F5.wireOp",EDGE,"E2.left");var subQ31=sQuery(id+"F5.wireOp",EDGE,"E2.right");var subQ33=sQuery(id+"F21.wireOp",EDGE,"E37.right");var subQ34=sQuery(id+"F25.wireOp",EDGE,"E41.bottom");var subQ35=sQuery(id+"F25.wireOp",EDGE,"E41.left");var subQ36=sQuery(id+"F21.wireOp",EDGE,"E36.bottom");var subQ37=sQuery(id+"F25.wireOp",EDGE,"E41.right");Q0=makeQuery(id+"F36.boolean.opBoolean","SPLIT",FACE,{"disambiguationData":[TD([makeQuery(id+"F32.opExtrude","SWEPT_FACE",FACE,{"disambiguationData":[OSD([subQ21])]})])],"derivedFrom":makeQuery(id+"F34.boolean.opBoolean","MERGE",FACE,{"derivedFrom":[makeQuery(id+"F32.opExtrude","CAP_FACE",FACE,{"disambiguationData":[OSD([subQ4,subQ2,subQ20,subQ21,subQ30,subQ31,subQ7,subQ36,subQ0,subQ23,subQ33,subQ34,subQ35,subQ37,sQuery(id+"F31.wireOp",EDGE,"E46.bottom"),sQuery(id+"F31.wireOp",EDGE,"E46.top"),sQuery(id+"F31.wireOp",EDGE,"E46.left"),sQuery(id+"F31.wireOp",EDGE,"E46.right")])],"isStart":true}),makeQuery(id+"F34.opExtrude","SWEPT_FACE",FACE,{"disambiguationData":[OSD([sQuery(id+"F33.wireOp",EDGE,"E47.bottom")])]})]})});}
            var sketch = newSketch(context, id + "F39", { "sketchPlane" : qUnion([Q0])});
            skLineSegment(sketch, "E54.bottom", {"start": v(271.64, -54.95) * mm, "end": v(316.62, -54.95) * mm});
            skLineSegment(sketch, "E54.top", {"start": v(271.64, -137.54) * mm, "end": v(316.62, -137.54) * mm});
            skLineSegment(sketch, "E54.left", {"start": v(271.64, -54.95) * mm, "end": v(271.64, -137.54) * mm});
            skLineSegment(sketch, "E54.right", {"start": v(316.62, -54.95) * mm, "end": v(316.62, -137.54) * mm});
            skSolve(sketch);
        }
        {
            var Q0;
            {var subQ0=sQuery(id+"F39.wireOp",EDGE,"E54.top");Q0=makeQuery(id+"F39.imprint","IMPRINT",FACE,{"disambiguationData":[TD([[makeQuery(id+"F39.imprint","IMPRINT",EDGE,{"derivedFrom":subQ0}),1.0]])]});}
            extrude(context, id + "F40", {"entities" : qUnion([Q0]), "operationType" : NewBodyOperationType.ADD, "depth" : 67.56 * mm});
        }
        {
            var Q0;
            Q0=makeQuery(id+"F38.opExtrude","SWEPT_FACE",FACE,{"disambiguationData":[OSD([sQuery(id+"F37.wireOp",EDGE,"E53.bottom")])]});
            var sketch = newSketch(context, id + "F41", { "sketchPlane" : qUnion([Q0])});
            skLineSegment(sketch, "E55", {"start": v(-301.36, -63.12) * mm, "end": v(-378.34, -63.12) * mm});
            skLineSegment(sketch, "E56", {"start": v(-305.34, -76.39) * mm, "end": v(-378.34, -76.39) * mm});
            skLineSegment(sketch, "E57", {"start": v(-378.34, -63.12) * mm, "end": v(-378.34, -76.39) * mm});
            skLineSegment(sketch, "E58", {"start": v(-296.72, -63.12) * mm, "end": v(-305.34, -76.39) * mm});
            skSolve(sketch);
        }
        {
            var Q0;
            {var subQ0=sQuery(id+"F41.wireOp",EDGE,"E57");Q0=makeQuery(id+"F41.imprint","IMPRINT",FACE,{"disambiguationData":[TD([[makeQuery(id+"F41.imprint","IMPRINT",EDGE,{"derivedFrom":subQ0}),1.0]])]});}
            var Q1;
            {var subQ0=sQuery(id+"F37.wireOp",EDGE,"E53.bottom");var subQ1=makeQuery(id+"F38.opExtrude","CAP_EDGE",EDGE,{"disambiguationData":[OSD([subQ0])],"isStart":false});Q1=makeQuery(id+"F41.imprint","IMPRINT",FACE,{"disambiguationData":[TD([[makeQuery(id+"F41.imprint","IMPRINT",EDGE,{"derivedFrom":subQ1}),1.0]])]});}
            extrude(context, id + "F42", {"entities" : qUnion([Q0, Q1]), "operationType" : NewBodyOperationType.ADD, "depth" : 25.4 * mm});
        }
        {
            var Q0;
            Q0=makeQuery(id+"F42.opExtrude","CAP_FACE",FACE,{"disambiguationData":[OSD([sQuery(id+"F37.wireOp",EDGE,"E53.bottom"),sQuery(id+"F37.wireOp",EDGE,"E53.left"),sQuery(id+"F37.wireOp",EDGE,"E53.right"),sQuery(id+"F41.wireOp",EDGE,"E55"),sQuery(id+"F41.wireOp",EDGE,"E56"),sQuery(id+"F41.wireOp",EDGE,"E57")])],"isStart":false});
            var sketch = newSketch(context, id + "F43", { "sketchPlane" : qUnion([Q0])});
            skLineSegment(sketch, "E59.bottom", {"start": v(-271.64, -61.65) * mm, "end": v(-233.42, -61.65) * mm});
            skLineSegment(sketch, "E59.top", {"start": v(-271.64, -71.52) * mm, "end": v(-233.42, -71.52) * mm});
            skLineSegment(sketch, "E59.left", {"start": v(-271.64, -61.65) * mm, "end": v(-271.64, -71.52) * mm});
            skLineSegment(sketch, "E59.right", {"start": v(-233.42, -61.65) * mm, "end": v(-233.42, -71.52) * mm});
            skSolve(sketch);
        }
        {
            var Q0;
            Q0=makeQuery(id+"F43.imprint","IMPRINT",FACE,{"disambiguationData":[TD([[makeQuery(id+"F43.imprint","IMPRINT",EDGE,{"derivedFrom":sQuery(id+"F43.wireOp",EDGE,"E59.bottom")}),-1.0]])]});
            extrude(context, id + "F44", {"entities" : qUnion([Q0]), "depth" : 25.4 * mm});
        }
    });
